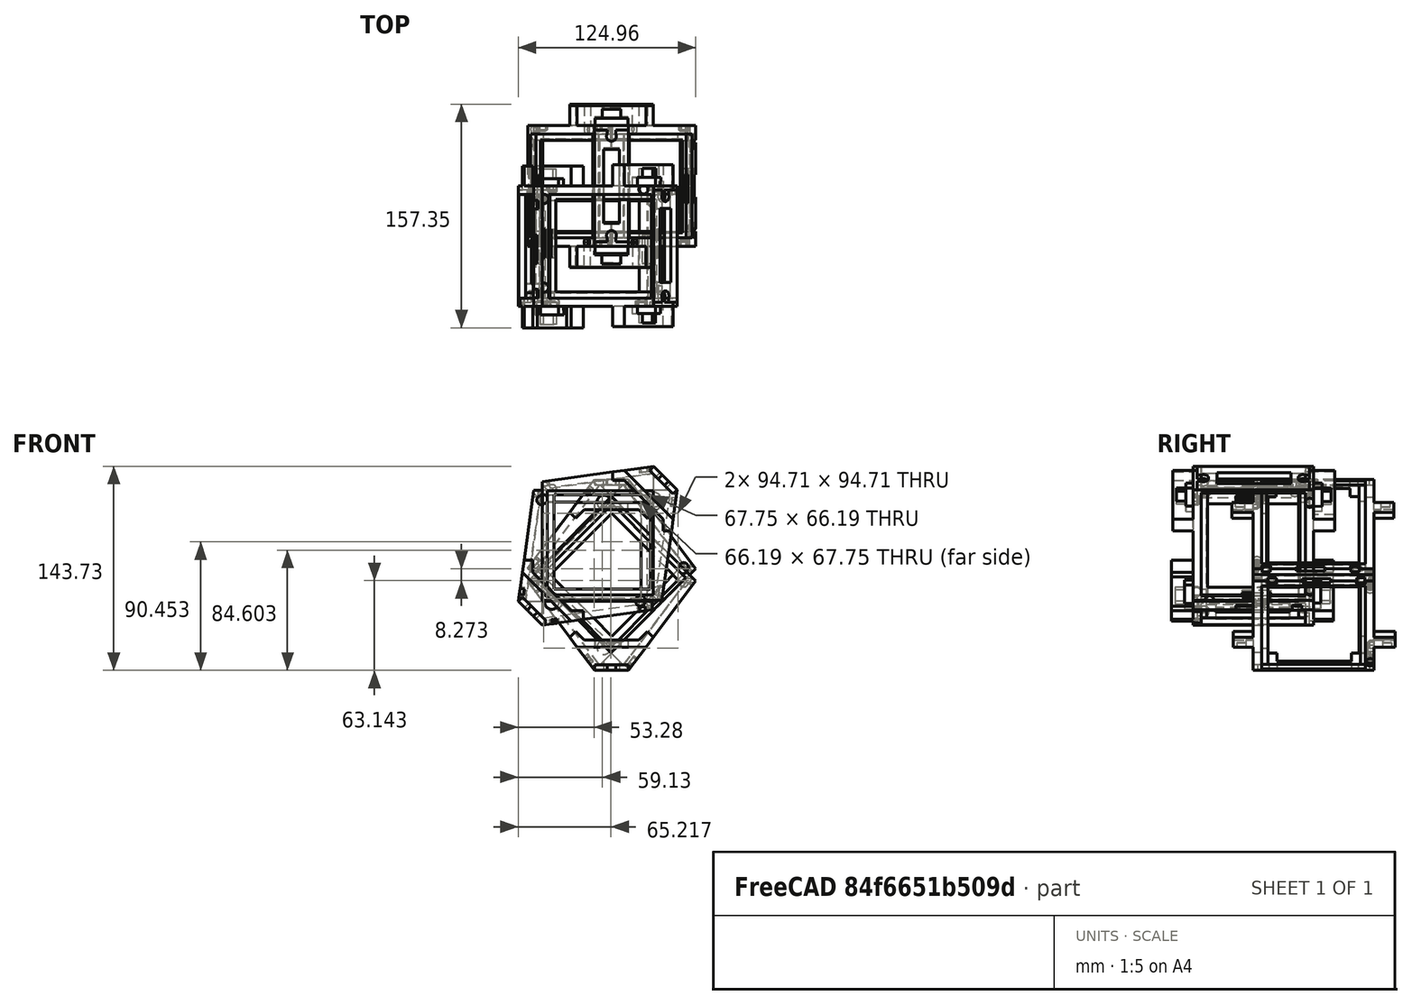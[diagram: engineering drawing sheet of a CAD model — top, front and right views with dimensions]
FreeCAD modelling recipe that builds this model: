
FCSTD DOCUMENT  (FreeCAD 0.21R33771 (Git))
Label: frame
License: All rights reserved
LicenseURL: http://en.wikipedia.org/wiki/All_rights_reserved
objects: Part::RuledSurface×12, Part::Feature×8, Part::Compound×5
note: 25 computed .brp shape members not serialized (recipe doc carries the construction recipe); baked Part::Feature solids carry a one-line shape summary decoded from their .brp

FEATURE [Part::Feature] Part__Feature  label="frame1"
  Placement = pos=(10.9897,-84.9,9.69316) rot=(0,0,1;0rad)
  shape: bbox 94.71 x 114 x 95.39 mm, 125 faces (baked)
FEATURE [Part::Feature] Part__Feature001  label="frame2"
  Placement = pos=(0.709798,1.42e-14,-0.586703) rot=(1,0,-1;3.14159rad)
  shape: bbox 95.39 x 114 x 94.71 mm, 125 faces (baked)
FEATURE [Part::Compound] Compound
  Links = -> [Part__Feature,Part__Feature001]
  Placement = pos=(-21.5084,42.45,7.10505) rot=(0,1,0;2.35619rad)
FEATURE [Part::RuledSurface] Ruled_Surface
  Curve1 = -> Compound [Edge162]
  Curve2 = -> Compound [Edge168]
  Orientation = 0
FEATURE [Part::RuledSurface] Ruled_Surface001
  Curve1 = -> Compound [Edge326]
  Curve2 = -> Compound [Edge107]
  Orientation = 0
FEATURE [Part::RuledSurface] Ruled_Surface002
  Curve1 = -> Compound [Edge507]
  Curve2 = -> Compound [Edge726]
  Orientation = 0
FEATURE [Part::RuledSurface] Ruled_Surface003
  Curve1 = -> Compound [Edge562]
  Curve2 = -> Compound [Edge568]
  Orientation = 0
FEATURE [Part::RuledSurface] Ruled_Surface004
  Curve1 = -> Compound [Edge130]
  Curve2 = -> Compound [Edge128]
  Orientation = 0
FEATURE [Part::RuledSurface] Ruled_Surface005
  Curve1 = -> Compound [Edge530]
  Curve2 = -> Compound [Edge528]
  Orientation = 0
FEATURE [Part::Feature] Part__Feature002  label="frame003"
  Placement = pos=(10.9897,-84.9,9.69316) rot=(0,0,1;0rad)
  shape: bbox 94.71 x 114 x 95.39 mm, 125 faces (baked)
FEATURE [Part::Feature] Part__Feature003  label="frame004"
  Placement = pos=(0.709798,1.4e-14,-0.586703) rot=(0.707107,0,-0.707107;3.14159rad)
  shape: bbox 95.39 x 114 x 94.71 mm, 125 faces (baked)
FEATURE [Part::Compound] Compound001
  Links = -> [Part__Feature002,Part__Feature003]
  Placement = pos=(-21.5084,42.45,7.10505) rot=(0,1,0;2.35619rad)
FEATURE [Part::Feature] Part__Feature004  label="frame005"
  Placement = pos=(10.9897,-84.9,9.69316) rot=(0,0,1;0rad)
  shape: bbox 94.71 x 114 x 95.39 mm, 125 faces (baked)
FEATURE [Part::Feature] Part__Feature005  label="frame006"
  Placement = pos=(0.709798,1.4e-14,-0.586703) rot=(0.707107,0,-0.707107;3.14159rad)
  shape: bbox 95.39 x 114 x 94.71 mm, 125 faces (baked)
FEATURE [Part::Compound] Compound002
  Links = -> [Part__Feature004,Part__Feature005]
  Placement = pos=(-21.5084,42.45,7.10505) rot=(0,1,0;2.35619rad)
FEATURE [Part::RuledSurface] Ruled_Surface006
  Curve1 = -> Compound002 [Edge162]
  Curve2 = -> Compound002 [Edge168]
  Orientation = 0
FEATURE [Part::RuledSurface] Ruled_Surface007
  Curve1 = -> Compound002 [Edge326]
  Curve2 = -> Compound002 [Edge107]
  Orientation = 0
FEATURE [Part::RuledSurface] Ruled_Surface008
  Curve1 = -> Compound002 [Edge507]
  Curve2 = -> Compound002 [Edge726]
  Orientation = 0
FEATURE [Part::RuledSurface] Ruled_Surface009
  Curve1 = -> Compound002 [Edge562]
  Curve2 = -> Compound002 [Edge568]
  Orientation = 0
FEATURE [Part::RuledSurface] Ruled_Surface010
  Curve1 = -> Compound002 [Edge130]
  Curve2 = -> Compound002 [Edge128]
  Orientation = 0
FEATURE [Part::RuledSurface] Ruled_Surface011
  Curve1 = -> Compound002 [Edge530]
  Curve2 = -> Compound002 [Edge528]
  Orientation = 0
FEATURE [Part::Compound] Compound003
  Links = -> [Ruled_Surface006,Ruled_Surface007,Ruled_Surface008,Ruled_Surface009,Ruled_Surface010,Ruled_Surface011]
FEATURE [Part::Compound] Compound004
  Links = -> [Compound001]
FEATURE [Part::Feature] Part__Feature006  label="frame007"
  Placement = pos=(10.9897,-84.9,9.69316) rot=(0,0,1;0rad)
  shape: bbox 94.71 x 114 x 95.39 mm, 125 faces (baked)
FEATURE [Part::Feature] Part__Feature007  label="frame008"
  Placement = pos=(0.709798,1.4e-14,-0.586703) rot=(0.707107,0,-0.707107;3.14159rad)
  shape: bbox 95.39 x 114 x 94.71 mm, 125 faces (baked)
